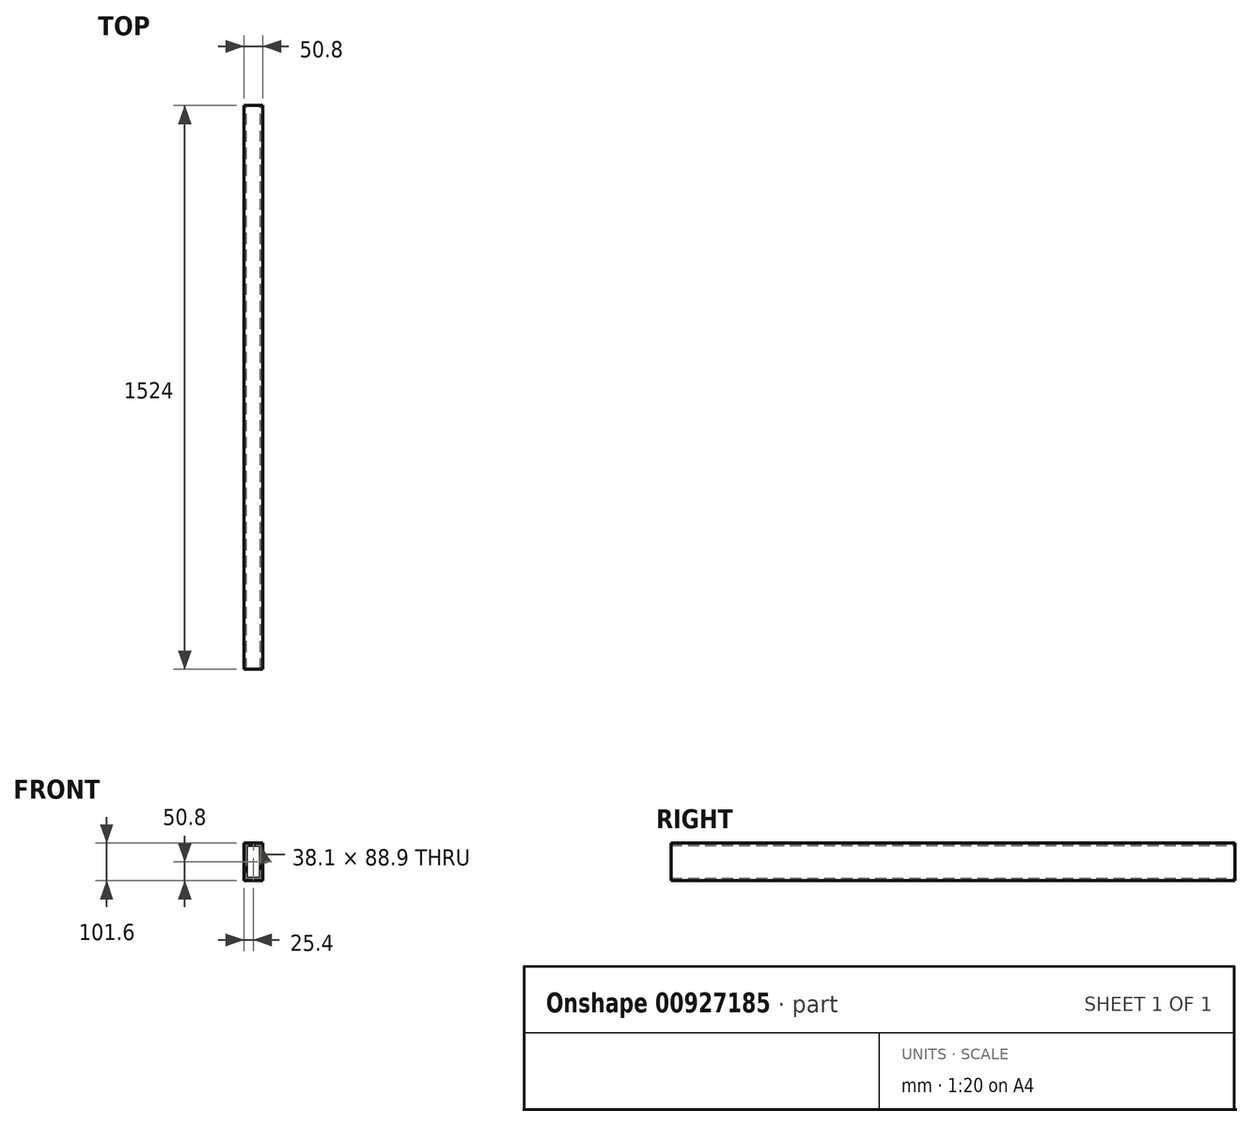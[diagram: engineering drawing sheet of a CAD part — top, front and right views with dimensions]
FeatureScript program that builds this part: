
annotation { "Feature Type Name" : "Feature", "Feature Type Description" : "" }
export const myFeature = defineFeature(function(context is Context, id is Id, definition is map)
    precondition{}
    {
        {
            var Q0;
            Q0=qCreatedBy(makeId("Front.planeOp"),FACE);
            var sketch = newSketch(context, id + "F0", { "sketchPlane" : qUnion([Q0])});
            skLineSegment(sketch, "E0.bottom", {"start": v(25.4, 50.8) * mm, "end": v(-25.4, 50.8) * mm});
            skLineSegment(sketch, "E0.top", {"start": v(25.4, -50.8) * mm, "end": v(-25.4, -50.8) * mm});
            skLineSegment(sketch, "E0.left", {"start": v(25.4, 50.8) * mm, "end": v(25.4, -50.8) * mm});
            skLineSegment(sketch, "E0.right", {"start": v(-25.4, 50.8) * mm, "end": v(-25.4, -50.8) * mm});
            skPoint(sketch, "E0.middle", {"position": v(0, 0) * mm});
            skLineSegment(sketch, "E1.0", {"start": v(19.05, 44.45) * mm, "end": v(-19.05, 44.45) * mm});
            skLineSegment(sketch, "E1.1", {"start": v(19.05, 44.45) * mm, "end": v(19.05, -44.45) * mm});
            skLineSegment(sketch, "E1.2", {"start": v(19.05, -44.45) * mm, "end": v(-19.05, -44.45) * mm});
            skLineSegment(sketch, "E1.3", {"start": v(-19.05, 44.45) * mm, "end": v(-19.05, -44.45) * mm});
            skSolve(sketch);
        }
        {
            var Q0;
            Q0 = qSketchRegion(id + "F0", true);
            extrude(context, id + "F1", {"entities" : qUnion([Q0]), "endBound" : BoundingType.SYMMETRIC, "depth" : 1524 * mm, "offsetDistance" : 25.4 * mm});
        }
    });
